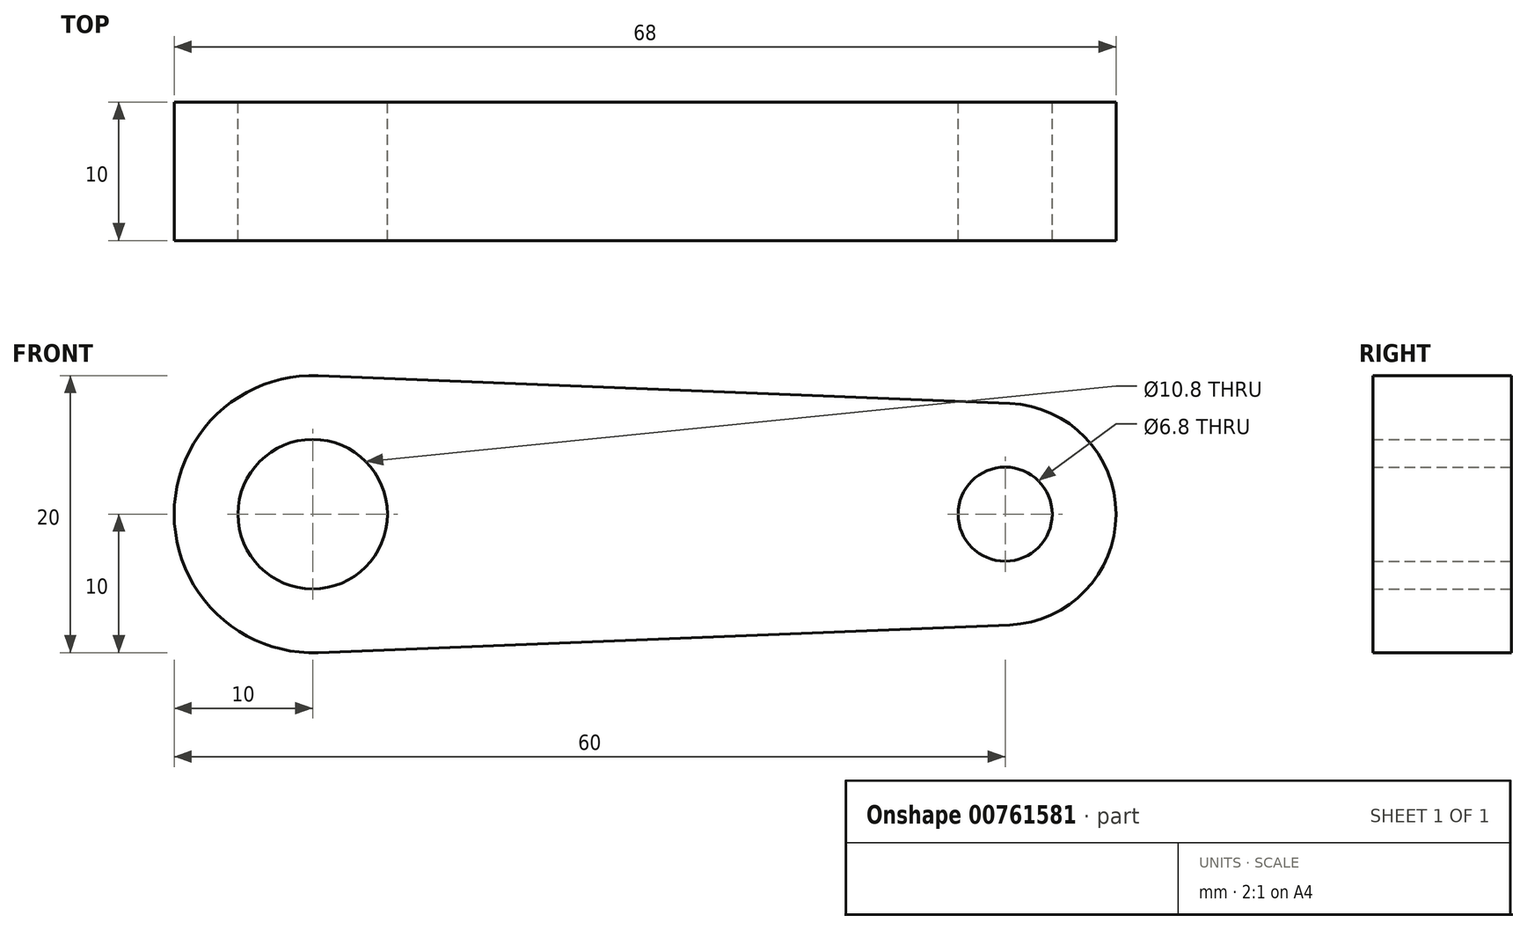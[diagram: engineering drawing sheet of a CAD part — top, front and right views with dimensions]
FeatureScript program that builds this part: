
annotation { "Feature Type Name" : "Feature", "Feature Type Description" : "" }
export const myFeature = defineFeature(function(context is Context, id is Id, definition is map)
    precondition{}
    {
        {
            var Q0;
            Q0=qCreatedBy(makeId("Front.planeOp"),FACE);
            var sketch = newSketch(context, id + "F0", { "sketchPlane" : qUnion([Q0])});
            skArc(sketch, "E0", {"start": v(0.4, 10) * mm, "mid": v(-10, 0) * mm, "end": v(0.4, -10) * mm});
            skArc(sketch, "E1", {"start": v(50.32, -8) * mm, "mid": v(58, 0) * mm, "end": v(50.32, 8) * mm});
            skLineSegment(sketch, "E2", {"start": v(0.4, 10) * mm, "end": v(50.32, 8) * mm});
            skLineSegment(sketch, "E3", {"start": v(0.4, -10) * mm, "end": v(50.32, -8) * mm});
            skSolve(sketch);
        }
        {
            var Q0;
            Q0 = qSketchRegion(id + "F0", true);
            extrude(context, id + "F1", {"entities" : qUnion([Q0]), "depth" : 10 * mm, "offsetDistance" : 25 * mm});
        }
        {
            var Q0;
            Q0=sQuery(id+"F0.wireOp",VERTEX,"E0.center");
            var Q1;
            Q1=makeQuery(id+"F1.opExtrude","SWEPT_BODY",BODY,{"disambiguationData":[OSD([sQuery(id+"F0.wireOp",EDGE,"E0"),sQuery(id+"F0.wireOp",EDGE,"E1"),sQuery(id+"F0.wireOp",EDGE,"E2"),sQuery(id+"F0.wireOp",EDGE,"E3")])]});
            hole(context, id + "F2", {"style" : HoleStyle.SIMPLE, "endStyle" : HoleEndStyle.THROUGH, "oppositeDirection" : true, "standardTappedOrClearance" : lookupTablePath({ "standard" : "ISO", "engagement" : "75%", "pitch" : "1.25 mm", "size" : "M12", "type" : "Tapped" }), "standardBlindInLast" : lookupTablePath({ "standard" : "ISO", "engagement" : "75%", "pitch" : "1.25 mm", "size" : "M12", "type" : "Tapped" }), "holeDiameter" : 10.8 * mm, "majorDiameter" : 12 * mm, "showTappedDepth" : true, "isTappedThrough" : true, "tappedDepth" : 7 * mm, "tapClearance" : 0, "startFromSketch" : true, "locations" : qUnion([Q0]), "scope" : qUnion([Q1])});
        }
        {
            var Q0;
            Q0=sQuery(id+"F0.wireOp",VERTEX,"E1.center");
            var Q1;
            Q1=makeQuery(id+"F1.opExtrude","SWEPT_BODY",BODY,{"disambiguationData":[OSD([sQuery(id+"F0.wireOp",EDGE,"E0"),sQuery(id+"F0.wireOp",EDGE,"E1"),sQuery(id+"F0.wireOp",EDGE,"E2"),sQuery(id+"F0.wireOp",EDGE,"E3")])]});
            hole(context, id + "F3", {"style" : HoleStyle.SIMPLE, "endStyle" : HoleEndStyle.THROUGH, "oppositeDirection" : true, "standardTappedOrClearance" : lookupTablePath({ "standard" : "ISO", "engagement" : "75%", "pitch" : "1.25 mm", "size" : "M8", "type" : "Tapped" }), "standardBlindInLast" : lookupTablePath({ "standard" : "ISO", "engagement" : "75%", "pitch" : "1.25 mm", "size" : "M8", "type" : "Tapped" }), "holeDiameter" : 6.8 * mm, "majorDiameter" : 8 * mm, "showTappedDepth" : true, "isTappedThrough" : true, "tappedDepth" : 7 * mm, "tapClearance" : 0, "startFromSketch" : true, "locations" : qUnion([Q0]), "scope" : qUnion([Q1])});
        }
    });
